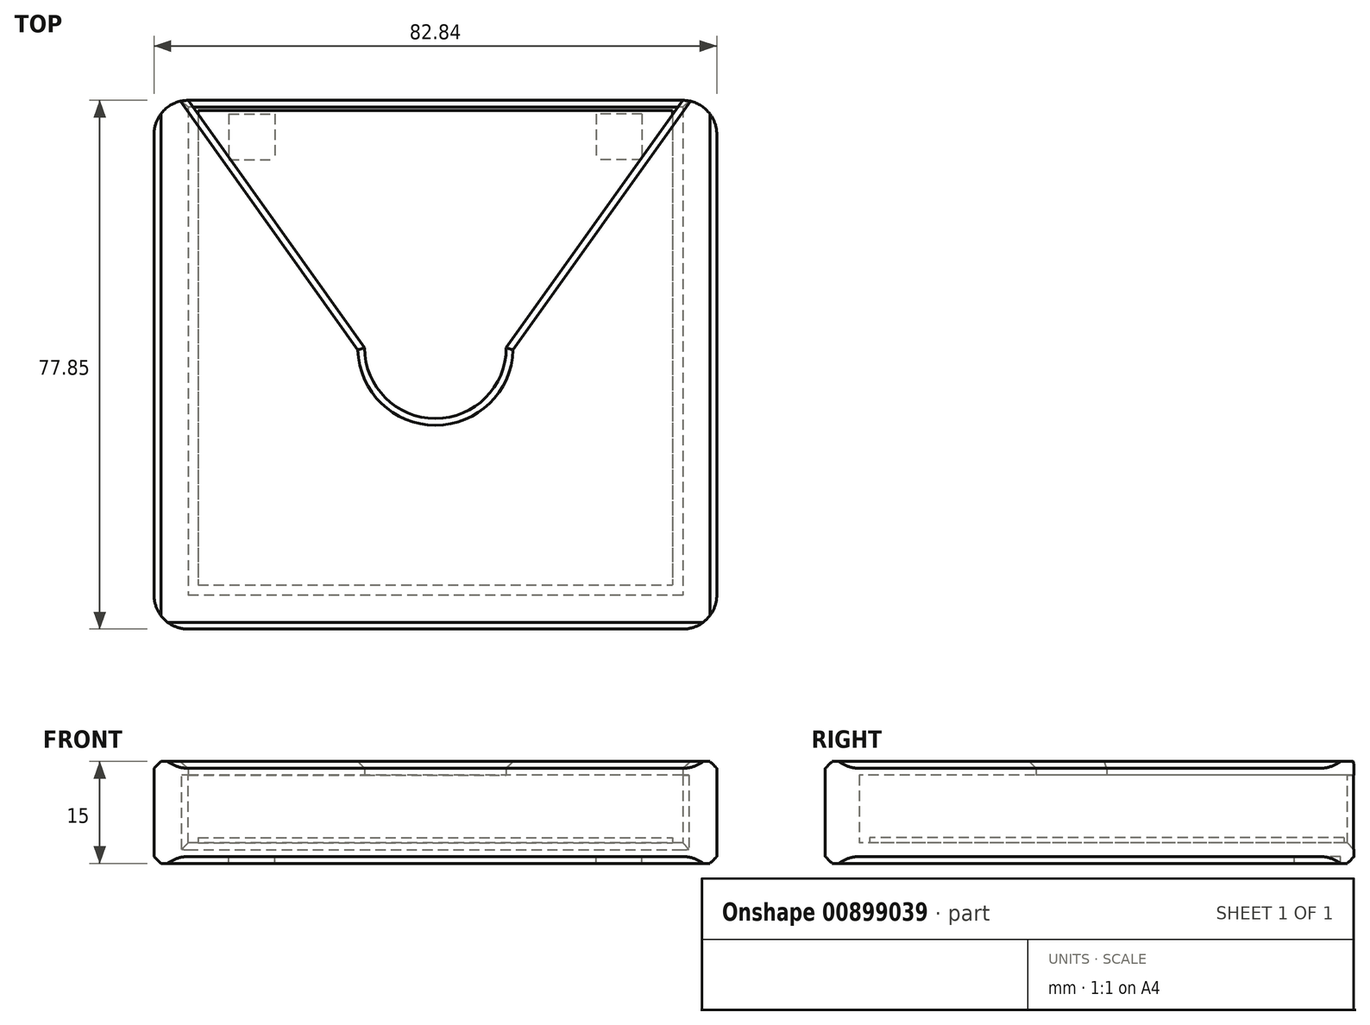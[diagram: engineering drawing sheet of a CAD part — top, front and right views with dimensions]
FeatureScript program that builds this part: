
annotation { "Feature Type Name" : "Feature", "Feature Type Description" : "" }
export const myFeature = defineFeature(function(context is Context, id is Id, definition is map)
    precondition{}
    {
        {
            var Q0;
            Q0=qCreatedBy(makeId("Top.planeOp"),FACE);
            var sketch = newSketch(context, id + "F0", { "sketchPlane" : qUnion([Q0])});
            skLineSegment(sketch, "E0.bottom", {"start": v(-34.93, 34.93) * mm, "end": v(34.93, 34.93) * mm});
            skLineSegment(sketch, "E0.top", {"start": v(-34.93, -34.93) * mm, "end": v(34.93, -34.92) * mm});
            skLineSegment(sketch, "E0.left", {"start": v(-34.93, 34.93) * mm, "end": v(-34.93, -34.93) * mm});
            skLineSegment(sketch, "E0.right", {"start": v(34.93, 34.93) * mm, "end": v(34.93, -34.93) * mm});
            skSolve(sketch);
        }
        {
            var Q0;
            Q0 = qSketchRegion(id + "F0", true);
            extrude(context, id + "F1", {"entities" : qUnion([Q0]), "depth" : 0.8 * mm, "offsetDistance" : 25 * mm});
        }
        {
            var Q0;
            Q0=qCreatedBy(makeId("Top.planeOp"),FACE);
            var sketch = newSketch(context, id + "F2", { "sketchPlane" : qUnion([Q0])});
            skLineSegment(sketch, "E1", {"start": v(-41.43, 36.43) * mm, "end": v(-36.43, 36.43) * mm});
            skLineSegment(sketch, "E2", {"start": v(-36.43, 36.43) * mm, "end": v(-36.43, -36.42) * mm});
            skLineSegment(sketch, "E3", {"start": v(-36.43, -36.42) * mm, "end": v(0, -36.42) * mm});
            skLineSegment(sketch, "E4", {"start": v(0, -41.42) * mm, "end": v(-41.42, -41.43) * mm});
            skLineSegment(sketch, "E5", {"start": v(-41.42, -41.43) * mm, "end": v(-41.42, 36.43) * mm});
            skPoint(sketch, "E6", {"position": v(0, -36.42) * mm});
            skPoint(sketch, "E7", {"position": v(0, -41.42) * mm});
            skLineSegment(sketch, "E8", {"start": v(0, -36.42) * mm, "end": v(0, -41.42) * mm, "construction": true});
            skLineSegment(sketch, "E9.MirrorCS", {"start": v(41.43, 36.43) * mm, "end": v(36.43, 36.43) * mm});
            skLineSegment(sketch, "E10.MirrorCS", {"start": v(36.43, 36.43) * mm, "end": v(36.43, -36.42) * mm});
            skLineSegment(sketch, "E11.MirrorCS", {"start": v(41.42, -41.43) * mm, "end": v(41.42, 36.43) * mm});
            skLineSegment(sketch, "E12.MirrorCS", {"start": v(36.43, -36.42) * mm, "end": v(0, -36.42) * mm});
            skLineSegment(sketch, "E13.MirrorCS", {"start": v(0, -41.42) * mm, "end": v(41.42, -41.43) * mm});
            skSolve(sketch);
        }
        {
            var Q0;
            Q0 = qSketchRegion(id + "F2", true);
            extrude(context, id + "F3", {"entities" : qUnion([Q0]), "depth" : 10 * mm, "offsetDistance" : 25 * mm});
        }
        {
            var Q0;
            Q0=makeQuery(id+"F3.opExtrude","CAP_FACE",FACE,{"disambiguationData":[OSD([sQuery(id+"F2.wireOp",EDGE,"E1"),sQuery(id+"F2.wireOp",EDGE,"E2"),sQuery(id+"F2.wireOp",EDGE,"E3"),sQuery(id+"F2.wireOp",EDGE,"E4"),sQuery(id+"F2.wireOp",EDGE,"E5"),sQuery(id+"F2.wireOp",EDGE,"E9.MirrorCS"),sQuery(id+"F2.wireOp",EDGE,"E10.MirrorCS"),sQuery(id+"F2.wireOp",EDGE,"E11.MirrorCS"),sQuery(id+"F2.wireOp",EDGE,"E12.MirrorCS"),sQuery(id+"F2.wireOp",EDGE,"E13.MirrorCS")])],"isStart":false});
            var sketch = newSketch(context, id + "F4", { "sketchPlane" : qUnion([Q0])});
            skLineSegment(sketch, "E14", {"start": v(-41.43, 36.43) * mm, "end": v(-36.43, 36.43) * mm});
            skLineSegment(sketch, "E15", {"start": v(-36.43, 36.43) * mm, "end": v(-10.42, 0) * mm});
            skLineSegment(sketch, "E16", {"start": v(-41.43, 36.43) * mm, "end": v(-41.42, -41.43) * mm});
            skLineSegment(sketch, "E17", {"start": v(-41.42, -41.43) * mm, "end": v(0, -41.42) * mm});
            skLineSegment(sketch, "E18", {"start": v(0, 0) * mm, "end": v(0, -10.43) * mm, "construction": true});
            skLineSegment(sketch, "E19", {"start": v(0, -10.43) * mm, "end": v(0, -41.42) * mm, "construction": true});
            skArc(sketch, "E20", {"start": v(-10.43, 0) * mm, "mid": v(-7.37, -7.37) * mm, "end": v(0, -10.43) * mm});
            skLineSegment(sketch, "E21.MirrorCS", {"start": v(36.43, 36.43) * mm, "end": v(10.42, 0) * mm});
            skLineSegment(sketch, "E22.MirrorCS", {"start": v(41.43, 36.43) * mm, "end": v(36.43, 36.43) * mm});
            skLineSegment(sketch, "E23.MirrorCS", {"start": v(41.43, 36.43) * mm, "end": v(41.42, -41.43) * mm});
            skLineSegment(sketch, "E24.MirrorCS", {"start": v(41.42, -41.43) * mm, "end": v(0, -41.42) * mm});
            skArc(sketch, "E25.MirrorCS", {"start": v(10.43, 0) * mm, "mid": v(7.37, -7.37) * mm, "end": v(0, -10.43) * mm});
            skSolve(sketch);
        }
        {
            var Q0;
            Q0 = qSketchRegion(id + "F4", true);
            extrude(context, id + "F5", {"entities" : qUnion([Q0]), "operationType" : NewBodyOperationType.ADD, "depth" : 2 * mm, "offsetDistance" : 25 * mm});
        }
        {
            var Q0;
            Q0=makeQuery(id+"F3.opExtrude","CAP_FACE",FACE,{"disambiguationData":[OSD([sQuery(id+"F2.wireOp",EDGE,"E1"),sQuery(id+"F2.wireOp",EDGE,"E2"),sQuery(id+"F2.wireOp",EDGE,"E3"),sQuery(id+"F2.wireOp",EDGE,"E4"),sQuery(id+"F2.wireOp",EDGE,"E5"),sQuery(id+"F2.wireOp",EDGE,"E9.MirrorCS"),sQuery(id+"F2.wireOp",EDGE,"E10.MirrorCS"),sQuery(id+"F2.wireOp",EDGE,"E11.MirrorCS"),sQuery(id+"F2.wireOp",EDGE,"E12.MirrorCS"),sQuery(id+"F2.wireOp",EDGE,"E13.MirrorCS")])],"isStart":true});
            var sketch = newSketch(context, id + "F6", { "sketchPlane" : qUnion([Q0])});
            skLineSegment(sketch, "E26", {"start": v(41.43, -36.43) * mm, "end": v(-41.43, -36.43) * mm});
            skLineSegment(sketch, "E27", {"start": v(-41.43, -36.43) * mm, "end": v(-41.42, 41.43) * mm});
            skLineSegment(sketch, "E28", {"start": v(-41.42, 41.43) * mm, "end": v(41.42, 41.43) * mm});
            skLineSegment(sketch, "E29", {"start": v(41.42, 41.43) * mm, "end": v(41.43, -36.43) * mm});
            skSolve(sketch);
        }
        {
            var Q0;
            Q0 = qSketchRegion(id + "F6", true);
            extrude(context, id + "F7", {"entities" : qUnion([Q0]), "depth" : 2 * mm, "offsetDistance" : 25 * mm});
        }
        {
            var Q0;
            Q0=makeQuery(id+"F3.opExtrude","SWEPT_BODY",BODY,{"disambiguationData":[OSD([sQuery(id+"F2.wireOp",EDGE,"E1"),sQuery(id+"F2.wireOp",EDGE,"E2"),sQuery(id+"F2.wireOp",EDGE,"E3"),sQuery(id+"F2.wireOp",EDGE,"E4"),sQuery(id+"F2.wireOp",EDGE,"E5"),sQuery(id+"F2.wireOp",EDGE,"E9.MirrorCS"),sQuery(id+"F2.wireOp",EDGE,"E10.MirrorCS"),sQuery(id+"F2.wireOp",EDGE,"E11.MirrorCS"),sQuery(id+"F2.wireOp",EDGE,"E12.MirrorCS"),sQuery(id+"F2.wireOp",EDGE,"E13.MirrorCS")])]});
            var Q1;
            Q1=makeQuery(id+"F7.opExtrude","SWEPT_BODY",BODY,{"disambiguationData":[OSD([sQuery(id+"F6.wireOp",EDGE,"E26"),sQuery(id+"F6.wireOp",EDGE,"E27"),sQuery(id+"F6.wireOp",EDGE,"E28"),sQuery(id+"F6.wireOp",EDGE,"E29")])]});
            booleanBodies(context, id + "F8", {"operationType" : BooleanOperationType.UNION, "tools" : qUnion([Q0, Q1])});
        }
        {
            var Q0;
            Q0=makeQuery(id+"F7.opExtrude","CAP_FACE",FACE,{"disambiguationData":[OSD([sQuery(id+"F6.wireOp",EDGE,"E26"),sQuery(id+"F6.wireOp",EDGE,"E27"),sQuery(id+"F6.wireOp",EDGE,"E28"),sQuery(id+"F6.wireOp",EDGE,"E29")])],"isStart":false});
            var sketch = newSketch(context, id + "F9", { "sketchPlane" : qUnion([Q0])});
            skLineSegment(sketch, "E30.bottom", {"start": v(29.42, -33.43) * mm, "end": v(24.66, -33.43) * mm, "construction": true});
            skLineSegment(sketch, "E30.top", {"start": v(29.42, -28.66) * mm, "end": v(24.66, -28.66) * mm, "construction": true});
            skLineSegment(sketch, "E30.left", {"start": v(29.42, -33.43) * mm, "end": v(29.42, -28.66) * mm, "construction": true});
            skLineSegment(sketch, "E30.right", {"start": v(24.66, -33.43) * mm, "end": v(24.66, -28.66) * mm, "construction": true});
            skLineSegment(sketch, "E31.bottom", {"start": v(30.42, -34.43) * mm, "end": v(23.66, -34.43) * mm});
            skLineSegment(sketch, "E31.top", {"start": v(30.42, -27.66) * mm, "end": v(23.66, -27.66) * mm});
            skLineSegment(sketch, "E31.left", {"start": v(30.42, -34.43) * mm, "end": v(30.42, -27.66) * mm});
            skLineSegment(sketch, "E31.right", {"start": v(23.66, -34.43) * mm, "end": v(23.66, -27.66) * mm});
            skLineSegment(sketch, "E32.MirrorCS", {"start": v(-30.42, -34.43) * mm, "end": v(-23.66, -34.43) * mm});
            skLineSegment(sketch, "E33.MirrorCS", {"start": v(-30.42, -34.43) * mm, "end": v(-30.42, -27.66) * mm});
            skLineSegment(sketch, "E34.MirrorCS", {"start": v(-30.42, -27.66) * mm, "end": v(-23.66, -27.66) * mm});
            skLineSegment(sketch, "E35.MirrorCS", {"start": v(-23.66, -34.43) * mm, "end": v(-23.66, -27.66) * mm});
            skLineSegment(sketch, "E36.bottom", {"start": v(41.43, -36.43) * mm, "end": v(-41.42, -36.43) * mm});
            skLineSegment(sketch, "E36.top", {"start": v(41.43, 41.43) * mm, "end": v(-41.42, 41.43) * mm});
            skLineSegment(sketch, "E36.left", {"start": v(41.43, -36.43) * mm, "end": v(41.43, 41.43) * mm});
            skLineSegment(sketch, "E36.right", {"start": v(-41.42, -36.43) * mm, "end": v(-41.42, 41.43) * mm});
            skSolve(sketch);
        }
        {
            var Q0;
            Q0 = qSketchRegion(id + "F9", true);
            extrude(context, id + "F10", {"entities" : qUnion([Q0]), "operationType" : NewBodyOperationType.ADD, "depth" : 1 * mm, "offsetDistance" : 25 * mm});
        }
        {
            var Q0;
            Q0=makeQuery(id+"F5.opExtrude","CAP_EDGE",EDGE,{"disambiguationData":[OSD([sQuery(id+"F4.wireOp",EDGE,"E16")])],"isStart":false});
            var Q1;
            Q1=makeQuery(id+"F5.opExtrude","CAP_EDGE",EDGE,{"disambiguationData":[OSD([sQuery(id+"F4.wireOp",EDGE,"E23.MirrorCS")])],"isStart":false});
            var Q2;
            Q2=makeQuery(id+"F10.opExtrude","CAP_EDGE",EDGE,{"disambiguationData":[OSD([sQuery(id+"F9.wireOp",EDGE,"E36.left")])],"isStart":false});
            var Q3;
            Q3=makeQuery(id+"F10.opExtrude","CAP_EDGE",EDGE,{"disambiguationData":[OSD([sQuery(id+"F9.wireOp",EDGE,"E36.right")])],"isStart":false});
            var Q4;
            Q4=makeQuery(id+"F10.opExtrude","CAP_EDGE",EDGE,{"disambiguationData":[OSD([sQuery(id+"F9.wireOp",EDGE,"E36.bottom")])],"isStart":false});
            var Q5;
            Q5=makeQuery(id+"F3.opExtrude","SWEPT_EDGE",EDGE,{"disambiguationData":[OSD([sQuery(id+"F2.wireOp",EDGE,"E1"),sQuery(id+"F2.wireOp",EDGE,"E2")])]});
            var Q6;
            Q6=makeQuery(id+"F7.opExtrude","CAP_EDGE",EDGE,{"disambiguationData":[OSD([sQuery(id+"F6.wireOp",EDGE,"E26")])],"isStart":true});
            var Q7;
            Q7=makeQuery(id+"F3.opExtrude","SWEPT_EDGE",EDGE,{"disambiguationData":[OSD([sQuery(id+"F2.wireOp",EDGE,"E9.MirrorCS"),sQuery(id+"F2.wireOp",EDGE,"E10.MirrorCS")])]});
            var Q8;
            Q8=makeQuery(id+"F5.opExtrude","CAP_EDGE",EDGE,{"disambiguationData":[OSD([sQuery(id+"F4.wireOp",EDGE,"E21.MirrorCS")])],"isStart":false});
            var Q9;
            Q9=makeQuery(id+"F5.opExtrude","CAP_EDGE",EDGE,{"disambiguationData":[OSD([sQuery(id+"F4.wireOp",EDGE,"E15")])],"isStart":false});
            var Q10;
            Q10=makeQuery(id+"F5.opExtrude","CAP_EDGE",EDGE,{"disambiguationData":[OSD([sQuery(id+"F4.wireOp",EDGE,"E20"),sQuery(id+"F4.wireOp",EDGE,"E25.MirrorCS")])],"isStart":false});
            var Q11;
            Q11=makeQuery(id+"F5.opExtrude","CAP_EDGE",EDGE,{"disambiguationData":[OSD([sQuery(id+"F4.wireOp",EDGE,"E17"),sQuery(id+"F4.wireOp",EDGE,"E24.MirrorCS")])],"isStart":false});
            var Q12;
            Q12=makeQuery(id+"F10.opExtrude","CAP_EDGE",EDGE,{"disambiguationData":[OSD([sQuery(id+"F9.wireOp",EDGE,"E36.top")])],"isStart":false});
            chamfer(context, id + "F11", {"entities" : qUnion([Q0, Q1, Q2, Q3, Q4, Q5, Q6, Q7, Q8, Q9, Q10, Q11, Q12]), "width" : 1 * mm, "tangentPropagation" : true});
        }
        {
            var Q0;
            Q0=makeQuery(id+"F10.boolean.opBoolean","MERGE",EDGE,{"derivedFrom":[makeQuery(id+"F8.opBoolean","MERGE",EDGE,{"derivedFrom":[makeQuery(id+"F5.boolean.opBoolean","MERGE",EDGE,{"derivedFrom":[makeQuery(id+"F3.opExtrude","SWEPT_EDGE",EDGE,{"disambiguationData":[OSD([sQuery(id+"F2.wireOp",EDGE,"E1"),sQuery(id+"F2.wireOp",EDGE,"E5")])]}),makeQuery(id+"F5.opExtrude","SWEPT_EDGE",EDGE,{"disambiguationData":[OSD([sQuery(id+"F4.wireOp",EDGE,"E14"),sQuery(id+"F4.wireOp",EDGE,"E16")])]})]}),makeQuery(id+"F7.opExtrude","SWEPT_EDGE",EDGE,{"disambiguationData":[OSD([sQuery(id+"F6.wireOp",EDGE,"E26"),sQuery(id+"F6.wireOp",EDGE,"E27")])]})]}),makeQuery(id+"F10.opExtrude","SWEPT_EDGE",EDGE,{"disambiguationData":[OSD([sQuery(id+"F9.wireOp",EDGE,"E36.bottom"),sQuery(id+"F9.wireOp",EDGE,"E36.right")])]})]});
            var Q1;
            Q1=makeQuery(id+"F10.boolean.opBoolean","MERGE",EDGE,{"derivedFrom":[makeQuery(id+"F8.opBoolean","MERGE",EDGE,{"derivedFrom":[makeQuery(id+"F5.boolean.opBoolean","MERGE",EDGE,{"derivedFrom":[makeQuery(id+"F3.opExtrude","SWEPT_EDGE",EDGE,{"disambiguationData":[OSD([sQuery(id+"F2.wireOp",EDGE,"E9.MirrorCS"),sQuery(id+"F2.wireOp",EDGE,"E11.MirrorCS")])]}),makeQuery(id+"F5.opExtrude","SWEPT_EDGE",EDGE,{"disambiguationData":[OSD([sQuery(id+"F4.wireOp",EDGE,"E22.MirrorCS"),sQuery(id+"F4.wireOp",EDGE,"E23.MirrorCS")])]})]}),makeQuery(id+"F7.opExtrude","SWEPT_EDGE",EDGE,{"disambiguationData":[OSD([sQuery(id+"F6.wireOp",EDGE,"E26"),sQuery(id+"F6.wireOp",EDGE,"E29")])]})]}),makeQuery(id+"F10.opExtrude","SWEPT_EDGE",EDGE,{"disambiguationData":[OSD([sQuery(id+"F9.wireOp",EDGE,"E36.bottom"),sQuery(id+"F9.wireOp",EDGE,"E36.left")])]})]});
            fillet(context, id + "F12", {"entities" : qUnion([Q0, Q1]), "radius" : 5 * mm, "tangentPropagation" : true, "allowEdgeOverflow" : false});
        }
        {
            var Q0;
            Q0=makeQuery(id+"F10.boolean.opBoolean","MERGE",EDGE,{"derivedFrom":[makeQuery(id+"F8.opBoolean","MERGE",EDGE,{"derivedFrom":[makeQuery(id+"F5.boolean.opBoolean","MERGE",EDGE,{"derivedFrom":[makeQuery(id+"F3.opExtrude","SWEPT_EDGE",EDGE,{"disambiguationData":[OSD([sQuery(id+"F2.wireOp",EDGE,"E11.MirrorCS"),sQuery(id+"F2.wireOp",EDGE,"E13.MirrorCS")])]}),makeQuery(id+"F5.opExtrude","SWEPT_EDGE",EDGE,{"disambiguationData":[OSD([sQuery(id+"F4.wireOp",EDGE,"E23.MirrorCS"),sQuery(id+"F4.wireOp",EDGE,"E24.MirrorCS")])]})]}),makeQuery(id+"F7.opExtrude","SWEPT_EDGE",EDGE,{"disambiguationData":[OSD([sQuery(id+"F6.wireOp",EDGE,"E28"),sQuery(id+"F6.wireOp",EDGE,"E29")])]})]}),makeQuery(id+"F10.opExtrude","SWEPT_EDGE",EDGE,{"disambiguationData":[OSD([sQuery(id+"F9.wireOp",EDGE,"E36.top"),sQuery(id+"F9.wireOp",EDGE,"E36.left")])]})]});
            var Q1;
            Q1=makeQuery(id+"F10.boolean.opBoolean","MERGE",EDGE,{"derivedFrom":[makeQuery(id+"F8.opBoolean","MERGE",EDGE,{"derivedFrom":[makeQuery(id+"F5.boolean.opBoolean","MERGE",EDGE,{"derivedFrom":[makeQuery(id+"F3.opExtrude","SWEPT_EDGE",EDGE,{"disambiguationData":[OSD([sQuery(id+"F2.wireOp",EDGE,"E4"),sQuery(id+"F2.wireOp",EDGE,"E5")])]}),makeQuery(id+"F5.opExtrude","SWEPT_EDGE",EDGE,{"disambiguationData":[OSD([sQuery(id+"F4.wireOp",EDGE,"E16"),sQuery(id+"F4.wireOp",EDGE,"E17")])]})]}),makeQuery(id+"F7.opExtrude","SWEPT_EDGE",EDGE,{"disambiguationData":[OSD([sQuery(id+"F6.wireOp",EDGE,"E27"),sQuery(id+"F6.wireOp",EDGE,"E28")])]})]}),makeQuery(id+"F10.opExtrude","SWEPT_EDGE",EDGE,{"disambiguationData":[OSD([sQuery(id+"F9.wireOp",EDGE,"E36.top"),sQuery(id+"F9.wireOp",EDGE,"E36.right")])]})]});
            fillet(context, id + "F13", {"entities" : qUnion([Q0, Q1]), "radius" : 5 * mm, "tangentPropagation" : true, "allowEdgeOverflow" : false});
        }
    });
